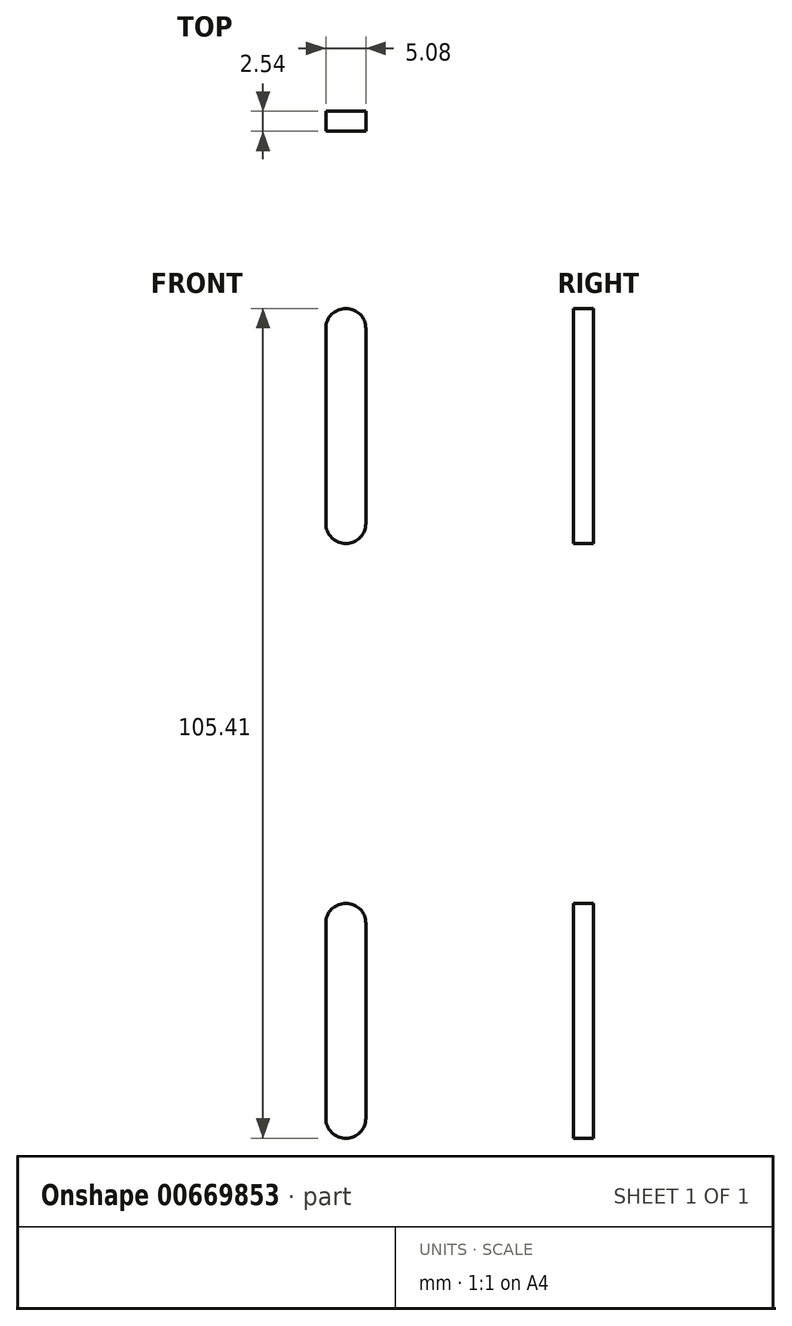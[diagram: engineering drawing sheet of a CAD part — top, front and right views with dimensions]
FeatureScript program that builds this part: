
annotation { "Feature Type Name" : "Feature", "Feature Type Description" : "" }
export const myFeature = defineFeature(function(context is Context, id is Id, definition is map)
    precondition{}
    {
        {
            var Q0;
            Q0=qCreatedBy(makeId("Front.planeOp"),FACE);
            var sketch = newSketch(context, id + "F0", { "sketchPlane" : qUnion([Q0])});
            skLineSegment(sketch, "E0.bottom", {"start": v(3.81, 0) * mm, "end": v(15.24, 0) * mm});
            skLineSegment(sketch, "E0.top", {"start": v(3.8, 120.65) * mm, "end": v(15.24, 120.65) * mm});
            skLineSegment(sketch, "E0.left", {"start": v(0, 3.81) * mm, "end": v(0, 116.84) * mm});
            skLineSegment(sketch, "E0.right", {"start": v(19.05, 3.81) * mm, "end": v(19.05, 116.84) * mm});
            skPoint(sketch, "E1.visualSharp", {"position": v(0, 120.65) * mm});
            skArc(sketch, "E1.filletArc", {"start": v(3.8, 120.65) * mm, "mid": v(1.12, 119.53) * mm, "end": v(0, 116.84) * mm});
            skPoint(sketch, "E2.visualSharp", {"position": v(19.05, 120.65) * mm});
            skArc(sketch, "E2.filletArc", {"start": v(19.05, 116.84) * mm, "mid": v(17.93, 119.53) * mm, "end": v(15.24, 120.65) * mm});
            skPoint(sketch, "E3.visualSharp", {"position": v(19.05, 0) * mm});
            skArc(sketch, "E3.filletArc", {"start": v(15.24, 0) * mm, "mid": v(17.93, 1.12) * mm, "end": v(19.05, 3.81) * mm});
            skPoint(sketch, "E4.visualSharp", {"position": v(0, 0) * mm});
            skArc(sketch, "E4.filletArc", {"start": v(0, 3.8) * mm, "mid": v(1.12, 1.12) * mm, "end": v(3.81, 0) * mm});
            skSolve(sketch);
        }
        {
            var Q0;
            Q0=qSketchRegion(id+"F0",true);
            extrude(context, id + "F1", {"entities" : qUnion([Q0]), "depth" : 2.54 * mm, "offsetDistance" : 25.4 * mm});
        }
        {
            var Q0;
            Q0=makeQuery(id+"F1.opExtrude","CAP_FACE",FACE,{"disambiguationData":[OSD([sQuery(id+"F0.wireOp",EDGE,"E0.bottom"),sQuery(id+"F0.wireOp",EDGE,"E0.top"),sQuery(id+"F0.wireOp",EDGE,"E0.left"),sQuery(id+"F0.wireOp",EDGE,"E0.right"),sQuery(id+"F0.wireOp",EDGE,"E1.filletArc"),sQuery(id+"F0.wireOp",EDGE,"E2.filletArc"),sQuery(id+"F0.wireOp",EDGE,"E3.filletArc"),sQuery(id+"F0.wireOp",EDGE,"E4.filletArc")])],"isStart":false});
            var sketch = newSketch(context, id + "F2", { "sketchPlane" : qUnion([Q0])});
            skLineSegment(sketch, "E5", {"start": v(9.52, 110.5) * mm, "end": v(9.52, 85.73) * mm});
            skLineSegment(sketch, "E6", {"start": v(0, 110.5) * mm, "end": v(19.05, 110.5) * mm, "construction": true});
            skLineSegment(sketch, "E7", {"start": v(19.05, 10.16) * mm, "end": v(0, 10.16) * mm, "construction": true});
            skLineSegment(sketch, "E8", {"start": v(9.52, 10.16) * mm, "end": v(9.52, 34.92) * mm});
            skArc(sketch, "E9.0.startCap", {"start": v(6.98, 110.5) * mm, "mid": v(9.52, 113.03) * mm, "end": v(12.06, 110.5) * mm});
            skArc(sketch, "E9.0.endCap", {"start": v(12.06, 85.73) * mm, "mid": v(9.52, 83.19) * mm, "end": v(6.98, 85.73) * mm});
            skLineSegment(sketch, "E9.0.left", {"start": v(12.06, 110.5) * mm, "end": v(12.06, 85.73) * mm});
            skLineSegment(sketch, "E9.0.right", {"start": v(6.98, 110.5) * mm, "end": v(6.98, 85.73) * mm});
            skArc(sketch, "E10.0.startCap", {"start": v(12.06, 10.16) * mm, "mid": v(9.52, 7.62) * mm, "end": v(6.98, 10.16) * mm});
            skArc(sketch, "E10.0.endCap", {"start": v(6.98, 34.92) * mm, "mid": v(9.52, 37.46) * mm, "end": v(12.06, 34.92) * mm});
            skLineSegment(sketch, "E10.0.left", {"start": v(6.98, 10.16) * mm, "end": v(6.98, 34.92) * mm});
            skLineSegment(sketch, "E10.0.right", {"start": v(12.06, 10.16) * mm, "end": v(12.06, 34.92) * mm});
            skSolve(sketch);
        }
        {
            var Q0;
            Q0=makeQuery(id+"F2.imprint","IMPRINT",FACE,{"disambiguationData":[TD([[makeQuery(id+"F2.imprint","IMPRINT",EDGE,{"derivedFrom":sQuery(id+"F2.wireOp",EDGE,"E9.0.startCap")}),-1.0]])]});
            var Q1;
            Q1=makeQuery(id+"F2.imprint","IMPRINT",FACE,{"disambiguationData":[TD([[makeQuery(id+"F2.imprint","IMPRINT",EDGE,{"derivedFrom":sQuery(id+"F2.wireOp",EDGE,"E10.0.startCap")}),-1.0]])]});
            extrude(context, id + "F3", {"entities" : qUnion([Q0, Q1]), "operationType" : NewBodyOperationType.REMOVE, "endBound" : BoundingType.THROUGH_ALL, "oppositeDirection" : true, "depth" : 25.4 * mm, "offsetDistance" : 25.4 * mm});
        }
    });
